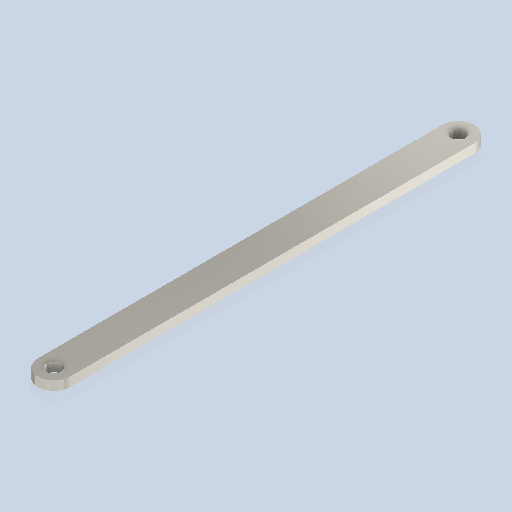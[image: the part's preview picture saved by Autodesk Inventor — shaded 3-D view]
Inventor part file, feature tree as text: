
AUTODESK INVENTOR PART (.ipt)
format: ipt  version: 2024.2 (Build 282272000, 272)  size: 249,344 bytes
history: native  units: mm
features: sketch x2, extrude x1, hole x1
ambient origin geometry x8: Origin, YZ Plane, XZ Plane, XY Plane, X Axis, Y Axis, Z Axis, Center Point
bodies: Volumenkörper1 (feature_tree)
feature tree (4):
  extrude  "Extrusion1"  Depth=3.5mm
  hole  "Bohrung1"  [1 undecoded]
  sketch  "Skizze1"  dims[d0=44.5mm d1=3.5mm]
  sketch  "Skizze2"  dims[d2=1.0mm d3=0.0mm d4=1.6mm d5=6.0mm d6=4.0mm d7=2.0mm d8=90.0deg d9=2.5mm d10=20.594885mm]
note: 1 required parameter value undecoded (feature->parameter linkage not recoverable at this tier; creation-order binding heuristic only, values carry confidence <= 0.55)
